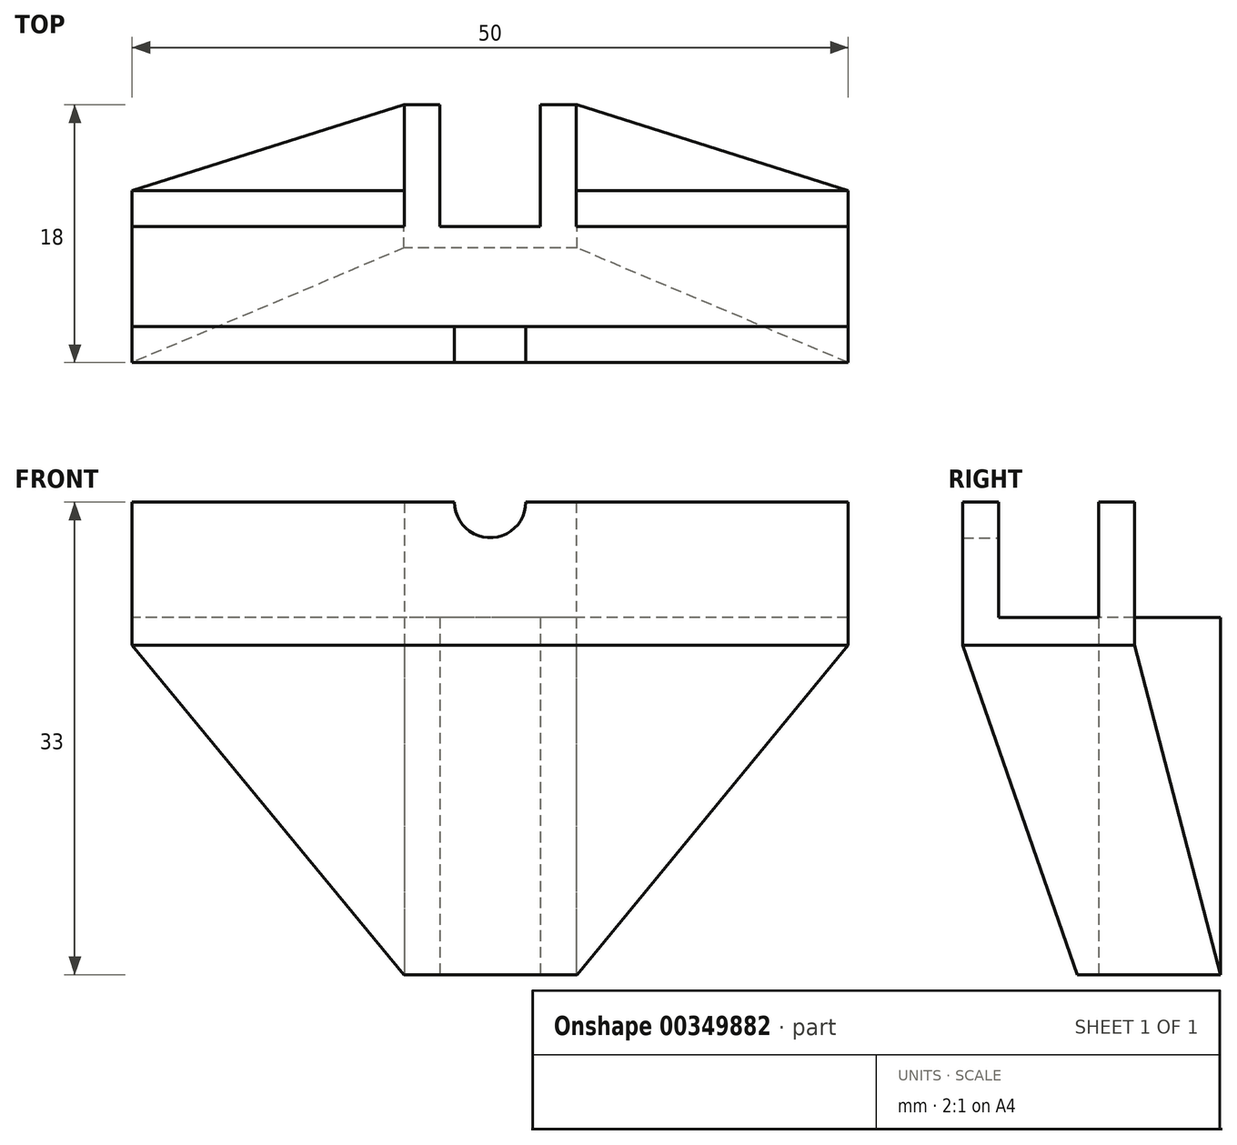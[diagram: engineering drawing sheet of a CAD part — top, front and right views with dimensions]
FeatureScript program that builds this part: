
annotation { "Feature Type Name" : "Feature", "Feature Type Description" : "" }
export const myFeature = defineFeature(function(context is Context, id is Id, definition is map)
    precondition{}
    {
        {
            var Q0;
            Q0=qCreatedBy(makeId("Right.planeOp"),FACE);
            var sketch = newSketch(context, id + "F0", { "sketchPlane" : qUnion([Q0])});
            skLineSegment(sketch, "E0", {"start": v(3, 16.5) * mm, "end": v(0.5, 16.5) * mm});
            skLineSegment(sketch, "E1", {"start": v(0.5, 16.5) * mm, "end": v(0.5, 8.44) * mm});
            skLineSegment(sketch, "E2", {"start": v(0.5, 8.44) * mm, "end": v(-6.5, 8.44) * mm});
            skLineSegment(sketch, "E3", {"start": v(-6.5, 8.44) * mm, "end": v(-6.5, 16.5) * mm});
            skLineSegment(sketch, "E4", {"start": v(-6.5, 16.5) * mm, "end": v(-9, 16.5) * mm});
            skLineSegment(sketch, "E5", {"start": v(-9, 16.5) * mm, "end": v(-9, 6.5) * mm});
            skLineSegment(sketch, "E6", {"start": v(-9, 6.5) * mm, "end": v(-1, -16.5) * mm});
            skLineSegment(sketch, "E7", {"start": v(-1, -16.5) * mm, "end": v(9, -16.5) * mm});
            skLineSegment(sketch, "E8", {"start": v(9, -16.5) * mm, "end": v(3, 6.5) * mm});
            skLineSegment(sketch, "E9", {"start": v(3, 6.5) * mm, "end": v(3, 16.5) * mm});
            skSolve(sketch);
        }
        {
            var Q0;
            Q0=qSketchRegion(id+"F0",true);
            extrude(context, id + "F1", {"entities" : qUnion([Q0]), "depth" : 25 * mm, "hasSecondDirection" : true, "secondDirectionOppositeDirection" : true, "secondDirectionDepth" : 25 * mm});
        }
        {
            var Q0;
            Q0=qCreatedBy(makeId("Top.planeOp"),FACE);
            var sketch = newSketch(context, id + "F2", { "sketchPlane" : qUnion([Q0])});
            skLineSegment(sketch, "E10.top", {"start": v(-6, 9) * mm, "end": v(-3.5, 9) * mm});
            skLineSegment(sketch, "E10.left", {"start": v(-6, 0.5) * mm, "end": v(-6, 9) * mm});
            skLineSegment(sketch, "E10.right", {"start": v(6, 0.5) * mm, "end": v(6, 9) * mm});
            skLineSegment(sketch, "E11.0", {"start": v(-3.5, 3) * mm, "end": v(-3.5, 9) * mm});
            skLineSegment(sketch, "E12.0", {"start": v(3.5, 3) * mm, "end": v(3.5, 9) * mm});
            skLineSegment(sketch, "E13.trimOffspring", {"start": v(3.5, 9) * mm, "end": v(6, 9) * mm});
            skLineSegment(sketch, "E14", {"start": v(-3.5, 9) * mm, "end": v(3.5, 9) * mm});
            skLineSegment(sketch, "E15", {"start": v(-3.5, 3) * mm, "end": v(-3.5, 0.5) * mm});
            skLineSegment(sketch, "E16", {"start": v(3.5, 3) * mm, "end": v(3.5, 0.5) * mm});
            skLineSegment(sketch, "E17", {"start": v(-6, 0.5) * mm, "end": v(-3.5, 0.5) * mm});
            skLineSegment(sketch, "E18", {"start": v(-3.5, 0.5) * mm, "end": v(3.5, 0.5) * mm});
            skLineSegment(sketch, "E19", {"start": v(3.5, 0.5) * mm, "end": v(6, 0.5) * mm});
            skSolve(sketch);
        }
        {
            var Q0;
            Q0=qSketchRegion(id+"F2",true);
            var Q1;
            Q1=makeQuery(id+"F1.opExtrude","SWEPT_FACE",FACE,{"disambiguationData":[OSD([sQuery(id+"F0.wireOp",EDGE,"E0")])]});
            var Q2;
            Q2=makeQuery(id+"F1.opExtrude","SWEPT_FACE",FACE,{"disambiguationData":[OSD([sQuery(id+"F0.wireOp",EDGE,"E7")])]});
            extrude(context, id + "F3", {"entities" : qUnion([Q0]), "operationType" : NewBodyOperationType.REMOVE, "endBound" : BoundingType.UP_TO_SURFACE, "endBoundEntityFace" : qUnion([Q1]), "depth" : 25 * mm, "hasSecondDirection" : true, "secondDirectionBound" : SecondDirectionBoundingType.UP_TO_SURFACE, "secondDirectionOppositeDirection" : true, "secondDirectionBoundEntityFace" : qUnion([Q2]), "secondDirectionDepth" : 25 * mm});
        }
        {
            var Q0;
            Q0=makeQuery(id+"F2.imprint","IMPRINT",FACE,{"disambiguationData":[TD([[makeQuery(id+"F2.imprint","IMPRINT",EDGE,{"derivedFrom":sQuery(id+"F2.wireOp",EDGE,"E10.top")}),-1.0]])]});
            var Q1;
            Q1=makeQuery(id+"F2.imprint","IMPRINT",FACE,{"disambiguationData":[TD([[makeQuery(id+"F2.imprint","IMPRINT",EDGE,{"derivedFrom":sQuery(id+"F2.wireOp",EDGE,"E10.right")}),1.0]])]});
            var Q2;
            Q2=makeQuery(id+"F1.opExtrude","SWEPT_FACE",FACE,{"disambiguationData":[OSD([sQuery(id+"F0.wireOp",EDGE,"E2")])]});
            var Q3;
            Q3=makeQuery(id+"F1.opExtrude","SWEPT_FACE",FACE,{"disambiguationData":[OSD([sQuery(id+"F0.wireOp",EDGE,"E7")])]});
            extrude(context, id + "F4", {"entities" : qUnion([Q0, Q1]), "operationType" : NewBodyOperationType.ADD, "endBound" : BoundingType.UP_TO_SURFACE, "endBoundEntityFace" : qUnion([Q2]), "depth" : 25 * mm, "hasSecondDirection" : true, "secondDirectionBound" : SecondDirectionBoundingType.UP_TO_SURFACE, "secondDirectionOppositeDirection" : true, "secondDirectionBoundEntityFace" : qUnion([Q3]), "secondDirectionDepth" : 25 * mm});
        }
        {
            var Q0;
            Q0=qCreatedBy(makeId("Front.planeOp"),FACE);
            var sketch = newSketch(context, id + "F5", { "sketchPlane" : qUnion([Q0])});
            skPoint(sketch, "E20", {"position": v(0, 16.5) * mm});
            skSolve(sketch);
        }
        {
            var Q0;
            Q0=sQuery(id+"F5.wireOp",VERTEX,"E20");
            var Q1;
            Q1=makeQuery(id+"F1.opExtrude","SWEPT_BODY",BODY,{"disambiguationData":[OSD([sQuery(id+"F0.wireOp",EDGE,"E0"),sQuery(id+"F0.wireOp",EDGE,"E1"),sQuery(id+"F0.wireOp",EDGE,"E2"),sQuery(id+"F0.wireOp",EDGE,"E3"),sQuery(id+"F0.wireOp",EDGE,"E4"),sQuery(id+"F0.wireOp",EDGE,"E5"),sQuery(id+"F0.wireOp",EDGE,"E6"),sQuery(id+"F0.wireOp",EDGE,"E7"),sQuery(id+"F0.wireOp",EDGE,"E8"),sQuery(id+"F0.wireOp",EDGE,"E9")])]});
            hole(context, id + "F6", {"style" : HoleStyle.SIMPLE, "endStyle" : HoleEndStyle.THROUGH, "oppositeDirection" : true, "holeDiameter" : 5 * mm, "isTappedThrough" : true, "tappedDepth" : 12 * mm, "tapClearance" : 3, "locations" : qUnion([Q0]), "scope" : qUnion([Q1])});
        }
        {
            var Q0;
            Q0=qCreatedBy(makeId("Front.planeOp"),FACE);
            var sketch = newSketch(context, id + "F7", { "sketchPlane" : qUnion([Q0])});
            skLineSegment(sketch, "E21", {"start": v(25, 6.5) * mm, "end": v(6.06, -16.5) * mm});
            skLineSegment(sketch, "E22", {"start": v(6.06, -16.5) * mm, "end": v(-6.01, -16.5) * mm});
            skLineSegment(sketch, "E23", {"start": v(-6.01, -16.5) * mm, "end": v(-25, 6.5) * mm});
            skLineSegment(sketch, "E24", {"start": v(-25, 6.5) * mm, "end": v(-25, 17.24) * mm});
            skLineSegment(sketch, "E25", {"start": v(-25, 17.24) * mm, "end": v(25, 17.24) * mm});
            skLineSegment(sketch, "E26", {"start": v(25, 17.24) * mm, "end": v(25, 6.5) * mm});
            skSolve(sketch);
        }
        {
            var Q0;
            Q0=qSketchRegion(id+"F7",true);
            extrude(context, id + "F8", {"entities" : qUnion([Q0]), "operationType" : NewBodyOperationType.INTERSECT, "depth" : 25 * mm, "hasSecondDirection" : true, "secondDirectionOppositeDirection" : true, "secondDirectionDepth" : 25 * mm});
        }
    });
